# Revit family: Building-IEC309Connections-GEWISS-44IB-INTERLOCKED-SOCKET-OUTLETS_IP44_WITHOUT_BOTTOM_FUS
name_source: partatom
category: Apparecchi elettrici
revit_build: Autodesk Revit 2016 (Build: 20161004_0715(x64)
units: mm (PartAtom-declared; Revit-internal decimal feet)

## family parameters
Condiviso = No
Host = Muro
Mantenere orientamento annotazione = Sì
Numero OmniClass = 23.80.50.14
Punto di calcolo locali = No
Quota connettore circolare = Usa diametro
Sempre verticale = Sì
Taglio con vuoti quando caricato = No
Tipo di parte = Normale
Titolo OmniClass = Plug Connectors

## types (22) — shared parameters
Altezza da terra = 820 mm
Carico apparente = 0 VA
Catalogue = BUILDING
Catalogue Range = 44 IB
Classificazione carico = Altro
Electrocod = 2220
Frequency = 50/60 Hz
Fuse breacking capacity = > 50 kA
Glow Wire Test = 850 °C (active parts) - 650 °C (passive parts)
Glow wire test: = 850 °C (active parts) - 650 °C (passive parts)
IDF = 220cc990-e7b6-467b-b248-952f9c972e44
IDT = d594ee1e-5beb-4100-9b20-8b248744bc80
IP degree = IP44
Immagine tipo = GW66132.jpg
Numero poli = 3
Operating temperature: = -25 +40 °C
Potenza = 500 V
Presa = GEWISS - NERO
Produttore = GEWISS S.p.A.
Protection = Fuse-holder base (CBF)
Rated frequency (Hz) = 50/60 Hz
SEO = Socket outlet
Shock resistance = IK08
Struttura = GEWISS - Grigio RAL - 7035
Technical sheet = https://www.gewiss.com
Thermo-pressure with ball = 125
Tipo simbolo = PRESAINDPFUS : 3P
Typology = Horizontal
URL = https://www.gewiss.com
Version file RFA = 18.0
Vetro = GEWISS - vetro
With back-mounting box = No
Working temperature = -25 ÷ +40 °C

## per-type parameters (varying)
| type | Colour | Colour: | Descrizione | EAN code | Fuses holder | Modello | No. of poles | Number of poles | Rated current (A) | Rated current (In) | Rated voltage | Reference h |
| GW66135 - 32A 3P+E 110V H.INT.SOCK.O.N.B. 4H CBF | Yellow | Yellow | 32A 3P+E 110V H.INT.SOCK.O.N.B. 4H CBF | 8011564029415 | E18 | GW66135 | 3P+E | 3P+E | 32 | 32 | 100-130V | 4 |
| GW66140 - 32A 2P+E 400V H.INT.SOCK.O.N.B. 9H CBF | Red | Red | 32A 2P+E 400V H.INT.SOCK.O.N.B. 9H CBF | 8011564029460 | E18 | GW66140 | 2P+E | 2P+E | 32 | 32 | 380-415V | 9 |
| GW66132 - 16A 3P+E 500V H.INT.SOCK.O.N.B. 7H CBF | Black | Black | 16A 3P+E 500V H.INT.SOCK.O.N.B. 7H CBF | 8011564029385 | gG | GW66132 | 3P+E | 3P+E | 16 | 16 | 480-500V | 7 |
| GW66137 - 32A 2P+E 230V H.INT.SOCK.O.N.B. 6H CBF | Blue | Blue | 32A 2P+E 230V H.INT.SOCK.O.N.B. 6H CBF | 8011564029439 | E18 | GW66137 | 2P+E | 2P+E | 32 | 32 | 200-250V | 6 |
| GW66130 - 16A 3P+E 400V H.INT.SOCK.O.N.B. 6H CBF | Red | Red | 16A 3P+E 400V H.INT.SOCK.O.N.B. 6H CBF | 8011564029361 | E14 | GW66130 | 3P+E | 3P+E | 16 | 16 | 380-415V | 6 |
| GW66139 - 32A 3P+N+E 230V H.INT.SOCK.O.N.B. 9H CBF | Blue | Blue | 32A 3P+N+E 230V H.INT.SOCK.O.N.B. 9H CBF | 8011564029453 | E18 | GW66139 | 3P+N+E | 3P+N+E | 32 | 32 | 200-250V | 9 |
| GW66124 - 16A 3P+E 110V H.INT.SOCK.O.N.B. 4H CBF | Yellow | Yellow | 16A 3P+E 110V H.INT.SOCK.O.N.B. 4H CBF | 8011564029309 | E14 | GW66124 | 3P+E | 3P+E | 16 | 16 | 100-130V | 4 |
| GW66144 - 32A 3P+N+E 500V H.INT.SOCK.O.N.B. 7H CBF | Black | Black | 32A 3P+N+E 500V H.INT.SOCK.O.N.B. 7H CBF | 8011564029507 | gG | GW66144 | 3P+N+E | 3P+N+E | 32 | 32 | 480-500V | 7 |
| GW66142 - 32A 3P+N+E 400V H.INT.SOCK.O.N.B. 6H CBF | Red | Red | 32A 3P+N+E 400V H.INT.SOCK.O.N.B. 6H CBF | 8011564029484 | E18 | GW66142 | 3P+N+E | 3P+N+E | 32 | 32 | 380-415V | 6 |
| GW66125 - 16A 3P+N+E 110V H.INT.SOCK.O.N.B. 4H CBF | Yellow | Yellow | 16A 3P+N+E 110V H.INT.SOCK.O.N.B. 4H CBF | 8011564029316 | E14 | GW66125 | 3P+N+E | 3P+N+E | 16 | 16 | 100-130V | 4 |
| GW66141 - 32A 3P+E 400V H.INT.SOCK.O.N.B. 6H CBF | Red | Red | 32A 3P+E 400V H.INT.SOCK.O.N.B. 6H CBF | 8011564029477 | E18 | GW66141 | 3P+E | 3P+E | 32 | 32 | 380-415V | 6 |
| GW66133 - 16A 3P+N+E 500V H.INT.SOCK.O.N.B. 7H CBF | Black | Black | 16A 3P+N+E 500V H.INT.SOCK.O.N.B. 7H CBF | 8011564029392 | gG | GW66133 | 3P+N+E | 3P+N+E | 16 | 16 | 480-500V | 7 |
| GW66127 - 16A 3P+E 230V H.INT.SOCK.O.N.B. 9H CBF | Blue | Blue | 16A 3P+E 230V H.INT.SOCK.O.N.B. 9H CBF | 8011564029330 | E14 | GW66127 | 3P+E | 3P+E | 16 | 16 | 200-250V | 9 |
| GW66134 - 32A 2P+E 110V H.INT.SOCK.O.N.B. 4H CBF | Yellow | Yellow | 32A 2P+E 110V H.INT.SOCK.O.N.B. 4H CBF | 8011564029408 | E18 | GW66134 | 2P+E | 2P+E | 32 | 32 | 100-130V | 4 |
| GW66138 - 32A 3P+E 230V H.INT.SOCK.O.N.B. 9H CBF | Blue | Blue | 32A 3P+E 230V H.INT.SOCK.O.N.B. 9H CBF | 8011564029446 | E18 | GW66138 | 3P+E | 3P+E | 32 | 32 | 200-250V | 9 |
| GW66143 - 32A 3P+E 500V H.INT.SOCK.O.N.B. 7H CBF | Black | Black | 32A 3P+E 500V H.INT.SOCK.O.N.B. 7H CBF | 8011564029491 | gG | GW66143 | 3P+E | 3P+E | 32 | 32 | 480-500V | 7 |
| GW66128 - 16A 3P+N+E 230V H.INT.SOCK.O.N.B. 9H CBF | Blue | Blue | 16A 3P+N+E 230V H.INT.SOCK.O.N.B. 9H CBF | 8011564029347 | E14 | GW66128 | 3P+N+E | 3P+N+E | 16 | 16 | 200-250V | 9 |
| GW66131 - 16A 3P+N+E 400V H.INT.SOCK.O.N.B. 6H CBF | Red | Red | 16A 3P+N+E 400V H.INT.SOCK.O.N.B. 6H CBF | 8011564029378 | E14 | GW66131 | 3P+N+E | 3P+N+E | 16 | 16 | 380-415V | 6 |
| GW66136 - 32A 3P+N+E 110V H.INT.SOCK.O.N.B. 4H CBF | Yellow | Yellow | 32A 3P+N+E 110V H.INT.SOCK.O.N.B. 4H CBF | 8011564029422 | E18 | GW66136 | 3P+N+E | 3P+N+E | 32 | 32 | 100-130V | 4 |
| GW66123 - 16A 2P+E 110V H.INT.SOCK.O.N.B. 4H CBF | Yellow | Yellow | 16A 2P+E 110V H.INT.SOCK.O.N.B. 4H CBF | 8011564029293 | E14 | GW66123 | 2P+E | 2P+E | 16 | 16 | 100-130V | 4 |
| GW66129 - 16A 2P+E 400V H.INT.SOCK.O.N.B. 9H CBF | Red | Red | 16A 2P+E 400V H.INT.SOCK.O.N.B. 9H CBF | 8011564029354 | E14 | GW66129 | 2P+E | 2P+E | 16 | 16 | 380-415V | 9 |
| GW66126 - 16A 2P+E 230V H.INT.SOCK.O.N.B. 6H CBF | Blue | Blue | 16A 2P+E 230V H.INT.SOCK.O.N.B. 6H CBF | 8011564029323 | E14 | GW66126 | 2P+E | 2P+E | 16 | 16 | 200-250V | 6 |

note: source unit labels omitted for Thermo-pressure with ball — the stored unit's dimension contradicts the parameter name (converter mislabeling)

## geometry (parser evidence)
native form markers: Blend x2, Sweep x1
no freeform markers — native parametric forms only
